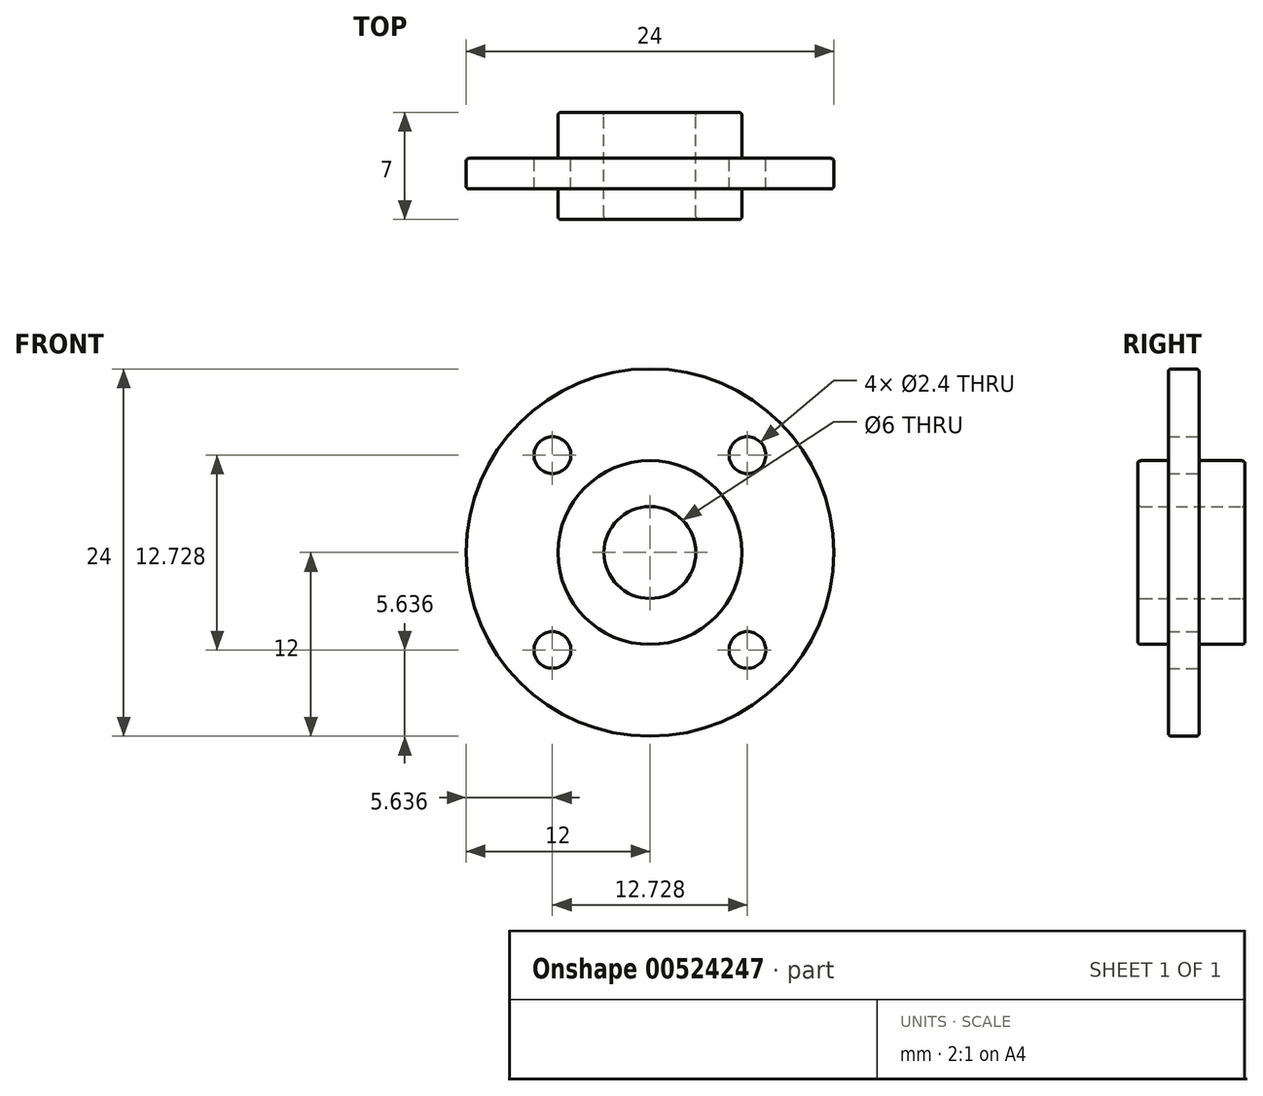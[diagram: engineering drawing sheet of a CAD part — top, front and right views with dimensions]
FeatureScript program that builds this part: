
annotation { "Feature Type Name" : "Feature", "Feature Type Description" : "" }
export const myFeature = defineFeature(function(context is Context, id is Id, definition is map)
    precondition{}
    {
        {
            var Q0;
            Q0=qCreatedBy(makeId("Front.planeOp"),FACE);
            var sketch = newSketch(context, id + "F0", { "sketchPlane" : qUnion([Q0])});
            skCircle(sketch, "E0", {"center": v(0, 0) * mm, "radius": 9 * mm, "construction": true});
            skCircle(sketch, "E1", {"center": v(0, 0) * mm, "radius": 12 * mm});
            skCircle(sketch, "E2", {"center": v(0, 0) * mm, "radius": 6 * mm});
            skCircle(sketch, "E3", {"center": v(0, 0) * mm, "radius": 3 * mm});
            skLineSegment(sketch, "E4", {"start": v(0, 12) * mm, "end": v(0, -12) * mm, "construction": true});
            skLineSegment(sketch, "E5", {"start": v(-12, 0) * mm, "end": v(12, 0) * mm, "construction": true});
            skLineSegment(sketch, "E6", {"start": v(-8.49, -8.49) * mm, "end": v(8.49, 8.49) * mm, "construction": true});
            skLineSegment(sketch, "E7", {"start": v(-8.49, 8.49) * mm, "end": v(8.49, -8.49) * mm, "construction": true});
            skCircle(sketch, "E8", {"center": v(-6.36, 6.36) * mm, "radius": 1.2 * mm});
            skCircle(sketch, "E9", {"center": v(6.36, 6.36) * mm, "radius": 1.2 * mm});
            skCircle(sketch, "E10", {"center": v(6.36, -6.36) * mm, "radius": 1.2 * mm});
            skCircle(sketch, "E11", {"center": v(-6.36, -6.36) * mm, "radius": 1.2 * mm});
            skSolve(sketch);
        }
        {
            var Q0;
            Q0=makeQuery(id+"F0.imprint","IMPRINT",FACE,{"disambiguationData":[TD([[makeQuery(id+"F0.imprint","IMPRINT",EDGE,{"derivedFrom":sQuery(id+"F0.wireOp",EDGE,"E1")}),1.0]])]});
            extrude(context, id + "F1", {"entities" : qUnion([Q0]), "depth" : 2 * mm, "offsetDistance" : 25 * mm});
        }
        {
            var Q0;
            Q0=makeQuery(id+"F0.imprint","IMPRINT",FACE,{"disambiguationData":[TD([[makeQuery(id+"F0.imprint","IMPRINT",EDGE,{"derivedFrom":sQuery(id+"F0.wireOp",EDGE,"E2")}),1.0]])]});
            extrude(context, id + "F2", {"entities" : qUnion([Q0]), "operationType" : NewBodyOperationType.ADD, "depth" : 4 * mm, "offsetDistance" : 25 * mm});
        }
        {
            var Q0;
            Q0=makeQuery(id+"F0.imprint","IMPRINT",FACE,{"disambiguationData":[TD([[makeQuery(id+"F0.imprint","IMPRINT",EDGE,{"derivedFrom":sQuery(id+"F0.wireOp",EDGE,"E2")}),1.0]])]});
            extrude(context, id + "F3", {"entities" : qUnion([Q0]), "operationType" : NewBodyOperationType.ADD, "oppositeDirection" : true, "depth" : 3 * mm, "offsetDistance" : 25 * mm});
        }
        {
            var Q0;
            Q0=makeQuery(id+"F2.opExtrude","CAP_EDGE",EDGE,{"disambiguationData":[OSD([sQuery(id+"F0.wireOp",EDGE,"E3")])],"isStart":false});
            var Q1;
            Q1=makeQuery(id+"F2.opExtrude","CAP_EDGE",EDGE,{"disambiguationData":[OSD([sQuery(id+"F0.wireOp",EDGE,"E2")])],"isStart":false});
            var Q2;
            Q2=makeQuery(id+"F1.opExtrude","CAP_EDGE",EDGE,{"disambiguationData":[OSD([sQuery(id+"F0.wireOp",EDGE,"E1")])],"isStart":false});
            var Q3;
            Q3=makeQuery(id+"F1.opExtrude","CAP_EDGE",EDGE,{"disambiguationData":[OSD([sQuery(id+"F0.wireOp",EDGE,"E1")])],"isStart":true});
            var Q4;
            Q4=makeQuery(id+"F3.opExtrude","CAP_EDGE",EDGE,{"disambiguationData":[OSD([sQuery(id+"F0.wireOp",EDGE,"E2")])],"isStart":false});
            var Q5;
            Q5=makeQuery(id+"F3.opExtrude","CAP_EDGE",EDGE,{"disambiguationData":[OSD([sQuery(id+"F0.wireOp",EDGE,"E3")])],"isStart":false});
            fillet(context, id + "F4", {"entities" : qUnion([Q0, Q1, Q2, Q3, Q4, Q5]), "radius" : 0.2 * mm, "tangentPropagation" : true, "allowEdgeOverflow" : false});
        }
    });
